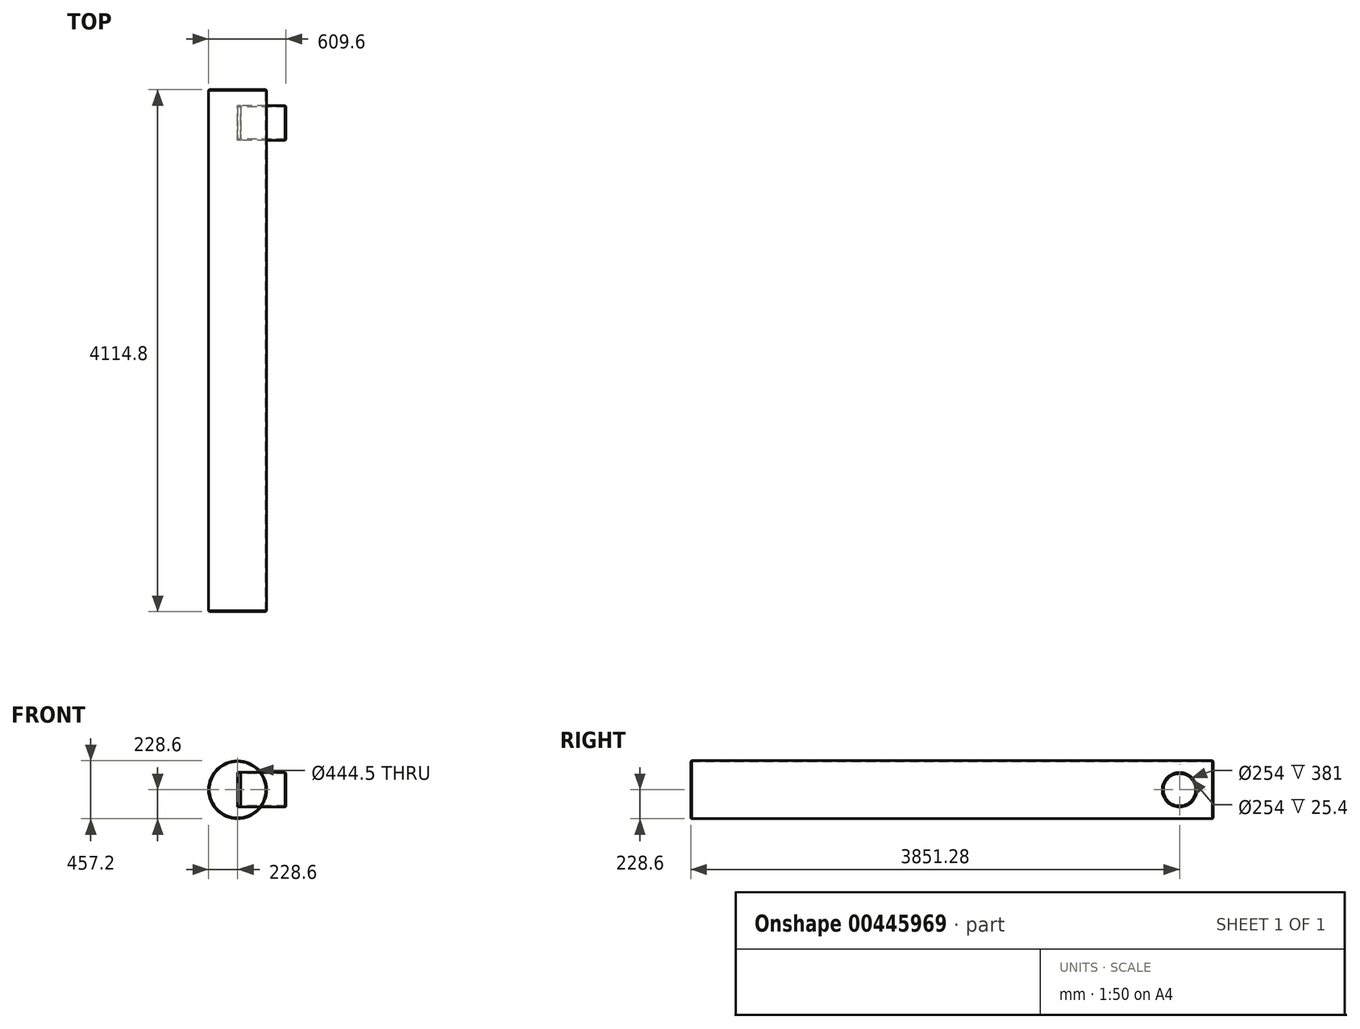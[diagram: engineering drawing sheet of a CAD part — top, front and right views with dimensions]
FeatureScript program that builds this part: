
annotation { "Feature Type Name" : "Feature", "Feature Type Description" : "" }
export const myFeature = defineFeature(function(context is Context, id is Id, definition is map)
    precondition{}
    {
        {
            var Q0;
            Q0=qCreatedBy(makeId("Front.planeOp"),FACE);
            var sketch = newSketch(context, id + "F0", { "sketchPlane" : qUnion([Q0])});
            skCircle(sketch, "E0", {"center": v(0, 0) * mm, "radius": 228.6 * mm});
            skCircle(sketch, "E1", {"center": v(0, 0) * mm, "radius": 222.25 * mm});
            skSolve(sketch);
        }
        {
            var Q0;
            Q0=makeQuery(id+"F0.imprint","IMPRINT",FACE,{"disambiguationData":[TD([[makeQuery(id+"F0.imprint","IMPRINT",EDGE,{"derivedFrom":sQuery(id+"F0.wireOp",EDGE,"E0")}),1.0]])]});
            extrude(context, id + "F1", {"entities" : qUnion([Q0]), "depth" : 4114.8 * mm, "offsetDistance" : 25.4 * mm});
        }
        {
            var Q0;
            Q0=makeQuery(id+"F1.opExtrude","CAP_EDGE",EDGE,{"disambiguationData":[OSD([sQuery(id+"F0.wireOp",EDGE,"E0")])],"isStart":false});
            chamfer(context, id + "F2", {"entities" : qUnion([Q0]), "width" : 6.35 * mm, "tangentPropagation" : true});
        }
        {
            var Q0;
            Q0=qCreatedBy(makeId("Right.planeOp"),FACE);
            var sketch = newSketch(context, id + "F3", { "sketchPlane" : qUnion([Q0])});
            skCircle(sketch, "E2", {"center": v(-263.53, 0) * mm, "radius": 127 * mm});
            skCircle(sketch, "E3", {"center": v(-263.53, 0) * mm, "radius": 136.53 * mm});
            skSolve(sketch);
        }
        {
            var Q0;
            Q0 = qSketchRegion(id + "F3", true);
            extrude(context, id + "F4", {"entities" : qUnion([Q0]), "depth" : 25.4 * mm, "offsetDistance" : 25.4 * mm});
        }
        {
            var Q0;
            Q0 = qSketchRegion(id + "F3", true);
            extrude(context, id + "F5", {"entities" : qUnion([Q0]), "depth" : 381 * mm, "offsetDistance" : 25.4 * mm});
        }
        {
            var Q0;
            Q0=makeQuery(id+"F5.opExtrude","CAP_EDGE",EDGE,{"disambiguationData":[OSD([sQuery(id+"F3.wireOp",EDGE,"E3")])],"isStart":false});
            chamfer(context, id + "F6", {"entities" : qUnion([Q0]), "width" : 6.35 * mm, "tangentPropagation" : true});
        }
        {
            var Q0;
            Q0=makeQuery(id+"F1.opExtrude","CAP_EDGE",EDGE,{"disambiguationData":[OSD([sQuery(id+"F0.wireOp",EDGE,"E0")])],"isStart":true});
            chamfer(context, id + "F7", {"entities" : qUnion([Q0]), "width" : 6.35 * mm, "tangentPropagation" : true});
        }
    });
